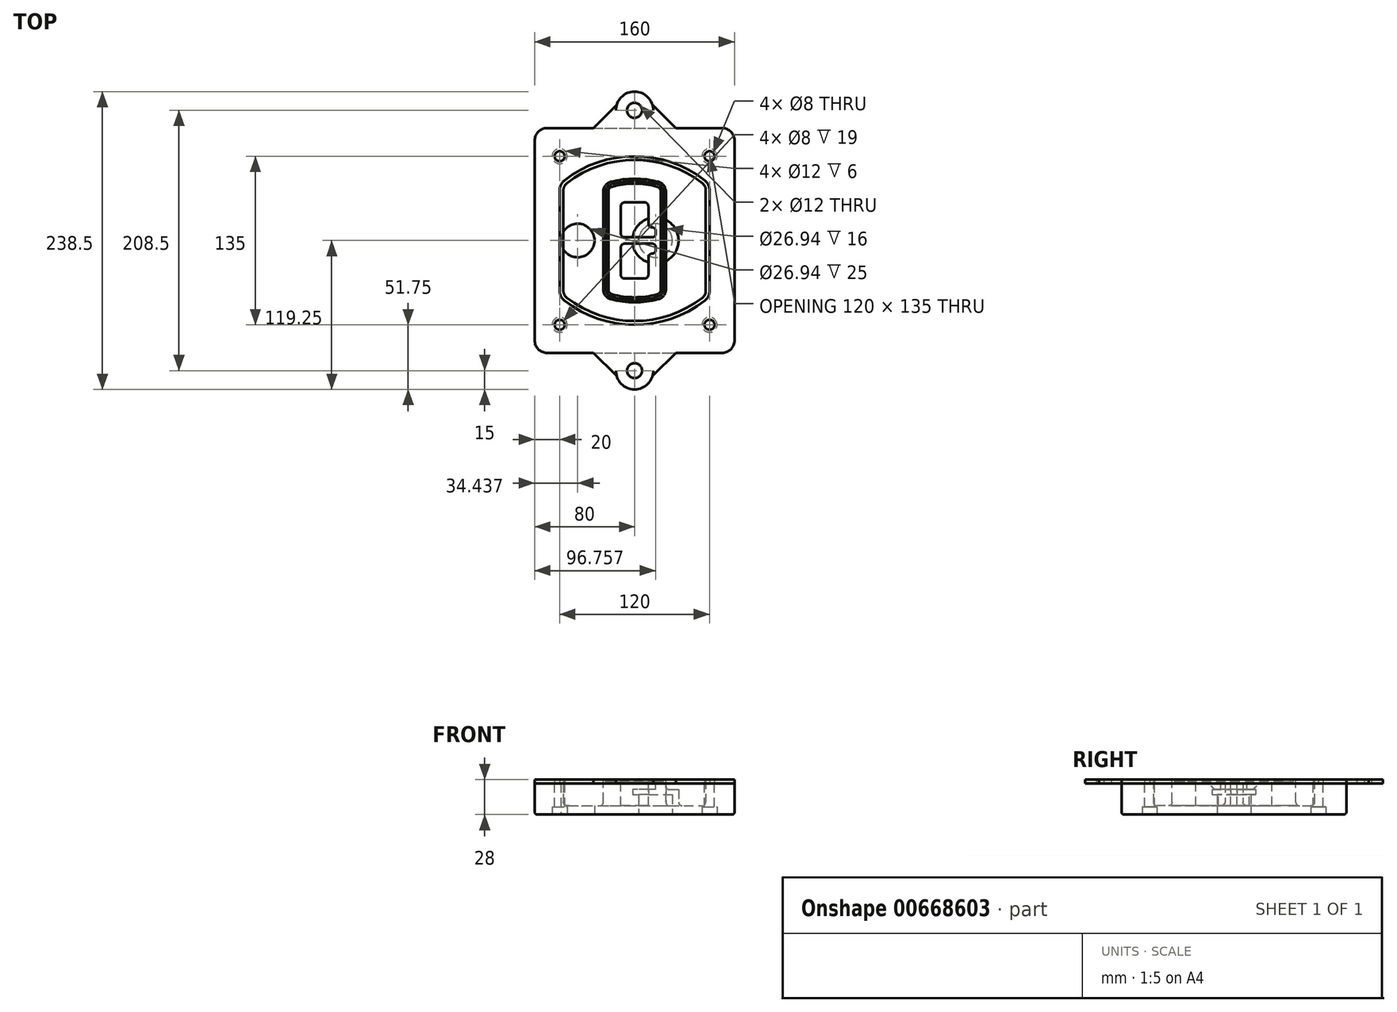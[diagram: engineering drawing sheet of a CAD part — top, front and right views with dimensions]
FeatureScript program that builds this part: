
annotation { "Feature Type Name" : "Feature", "Feature Type Description" : "" }
export const myFeature = defineFeature(function(context is Context, id is Id, definition is map)
    precondition{}
    {
        {
            var Q0;
            Q0=qCreatedBy(makeId("Top.planeOp"),FACE);
            var sketch = newSketch(context, id + "F0", { "sketchPlane" : qUnion([Q0])});
            skPoint(sketch, "E0.rect.middle", {"position": v(0, 0) * mm});
            skLineSegment(sketch, "E1.bottom", {"start": v(-70, -90) * mm, "end": v(70, -90) * mm});
            skLineSegment(sketch, "E1.top", {"start": v(-70, 90) * mm, "end": v(70, 90) * mm});
            skLineSegment(sketch, "E1.left", {"start": v(-80, -80) * mm, "end": v(-80, 80) * mm});
            skLineSegment(sketch, "E1.right", {"start": v(80, -80) * mm, "end": v(80, 80) * mm});
            skLineSegment(sketch, "E2", {"start": v(-80, 90) * mm, "end": v(80, -90) * mm, "construction": true});
            skLineSegment(sketch, "E3", {"start": v(80, 90) * mm, "end": v(-80, -90) * mm, "construction": true});
            skCircle(sketch, "E4", {"center": v(-60, 67.5) * mm, "radius": 4 * mm});
            skCircle(sketch, "E5", {"center": v(60, 67.5) * mm, "radius": 4 * mm});
            skCircle(sketch, "E6", {"center": v(60, -67.5) * mm, "radius": 4 * mm});
            skCircle(sketch, "E7", {"center": v(-60, -67.5) * mm, "radius": 4 * mm});
            skLineSegment(sketch, "E8", {"start": v(-60, 67.5) * mm, "end": v(60, 67.5) * mm, "construction": true});
            skLineSegment(sketch, "E9", {"start": v(60, 67.5) * mm, "end": v(60, -67.5) * mm, "construction": true});
            skLineSegment(sketch, "E10", {"start": v(60, -67.5) * mm, "end": v(-60, -67.5) * mm, "construction": true});
            skLineSegment(sketch, "E11", {"start": v(-60, -67.5) * mm, "end": v(-60, 67.5) * mm, "construction": true});
            skLineSegment(sketch, "E12", {"start": v(-60, 40.3) * mm, "end": v(-60, -40.3) * mm});
            skLineSegment(sketch, "E13", {"start": v(60, 40.3) * mm, "end": v(60, -40.3) * mm});
            skArc(sketch, "E14", {"start": v(56.15, 48.18) * mm, "mid": v(0, 67.5) * mm, "end": v(-56.15, 48.18) * mm});
            skArc(sketch, "E15", {"start": v(-56.15, -48.18) * mm, "mid": v(0, -67.5) * mm, "end": v(56.15, -48.18) * mm});
            skLineSegment(sketch, "E16", {"start": v(-60, 0) * mm, "end": v(60, 0) * mm, "construction": true});
            skPoint(sketch, "E17.visualSharp", {"position": v(-60, -45) * mm});
            skArc(sketch, "E17.filletArc", {"start": v(-60, -40.3) * mm, "mid": v(-58.99, -44.68) * mm, "end": v(-56.15, -48.18) * mm});
            skPoint(sketch, "E18.visualSharp", {"position": v(-60, 45) * mm});
            skArc(sketch, "E18.filletArc", {"start": v(-56.15, 48.18) * mm, "mid": v(-58.99, 44.68) * mm, "end": v(-60, 40.3) * mm});
            skPoint(sketch, "E19.visualSharp", {"position": v(60, 45) * mm});
            skArc(sketch, "E19.filletArc", {"start": v(60, 40.3) * mm, "mid": v(58.99, 44.68) * mm, "end": v(56.15, 48.18) * mm});
            skPoint(sketch, "E20.visualSharp", {"position": v(60, -45) * mm});
            skArc(sketch, "E20.filletArc", {"start": v(56.15, -48.18) * mm, "mid": v(58.99, -44.68) * mm, "end": v(60, -40.3) * mm});
            skPoint(sketch, "E21.visualSharp", {"position": v(-80, 90) * mm});
            skArc(sketch, "E21.filletArc", {"start": v(-70, 90) * mm, "mid": v(-77.07, 87.07) * mm, "end": v(-80, 80) * mm});
            skPoint(sketch, "E22.visualSharp", {"position": v(80, 90) * mm});
            skArc(sketch, "E22.filletArc", {"start": v(80, 80) * mm, "mid": v(77.07, 87.07) * mm, "end": v(70, 90) * mm});
            skPoint(sketch, "E23.visualSharp", {"position": v(80, -90) * mm});
            skArc(sketch, "E23.filletArc", {"start": v(70, -90) * mm, "mid": v(77.07, -87.07) * mm, "end": v(80, -80) * mm});
            skPoint(sketch, "E24.visualSharp", {"position": v(-80, -90) * mm});
            skArc(sketch, "E24.filletArc", {"start": v(-80, -80) * mm, "mid": v(-77.07, -87.07) * mm, "end": v(-70, -90) * mm});
            skArc(sketch, "E25.0", {"start": v(57, 40.3) * mm, "mid": v(56.3, 43.36) * mm, "end": v(54.3, 45.81) * mm});
            skLineSegment(sketch, "E25.1", {"start": v(57, 40.3) * mm, "end": v(57, -40.3) * mm});
            skArc(sketch, "E25.2", {"start": v(54.3, -45.81) * mm, "mid": v(56.3, -43.36) * mm, "end": v(57, -40.3) * mm});
            skArc(sketch, "E25.3", {"start": v(-54.3, -45.81) * mm, "mid": v(0, -64.5) * mm, "end": v(54.3, -45.81) * mm});
            skArc(sketch, "E25.4", {"start": v(-57, -40.3) * mm, "mid": v(-56.3, -43.36) * mm, "end": v(-54.3, -45.81) * mm});
            skArc(sketch, "E25.5", {"start": v(54.3, 45.81) * mm, "mid": v(0, 64.5) * mm, "end": v(-54.3, 45.81) * mm});
            skLineSegment(sketch, "E25.6", {"start": v(-57, 40.3) * mm, "end": v(-57, -40.3) * mm});
            skArc(sketch, "E25.7", {"start": v(-54.3, 45.81) * mm, "mid": v(-56.3, 43.36) * mm, "end": v(-57, 40.3) * mm});
            skArc(sketch, "E26.0", {"start": v(-58.62, 51.33) * mm, "mid": v(-62.58, 46.43) * mm, "end": v(-64, 40.3) * mm});
            skArc(sketch, "E26.1", {"start": v(58.62, 51.33) * mm, "mid": v(0, 71.5) * mm, "end": v(-58.62, 51.33) * mm});
            skArc(sketch, "E26.2", {"start": v(64, 40.3) * mm, "mid": v(62.58, 46.43) * mm, "end": v(58.62, 51.33) * mm});
            skLineSegment(sketch, "E26.3", {"start": v(64, 40.3) * mm, "end": v(64, -40.3) * mm});
            skArc(sketch, "E26.4", {"start": v(58.62, -51.33) * mm, "mid": v(62.58, -46.43) * mm, "end": v(64, -40.3) * mm});
            skLineSegment(sketch, "E26.5", {"start": v(-64, 40.3) * mm, "end": v(-64, -40.3) * mm});
            skArc(sketch, "E26.6", {"start": v(-58.62, -51.33) * mm, "mid": v(0, -71.5) * mm, "end": v(58.62, -51.33) * mm});
            skArc(sketch, "E26.7", {"start": v(-64, -40.3) * mm, "mid": v(-62.58, -46.43) * mm, "end": v(-58.62, -51.33) * mm});
            skSolve(sketch);
        }
        {
            var Q0;
            Q0=makeQuery(id+"F0.imprint","IMPRINT",FACE,{"disambiguationData":[TD([[makeQuery(id+"F0.imprint","IMPRINT",EDGE,{"derivedFrom":sQuery(id+"F0.wireOp",EDGE,"E1.bottom")}),1.0]])]});
            var Q1;
            Q1=makeQuery(id+"F0.imprint","IMPRINT",FACE,{"disambiguationData":[TD([[makeQuery(id+"F0.imprint","IMPRINT",EDGE,{"derivedFrom":sQuery(id+"F0.wireOp",EDGE,"E12")}),1.0]])]});
            var Q2;
            Q2=makeQuery(id+"F0.imprint","IMPRINT",FACE,{"disambiguationData":[TD([[makeQuery(id+"F0.imprint","IMPRINT",EDGE,{"derivedFrom":sQuery(id+"F0.wireOp",EDGE,"E25.0")}),1.0]])]});
            var Q3;
            Q3=makeQuery(id+"F0.imprint","IMPRINT",FACE,{"disambiguationData":[TD([[makeQuery(id+"F0.imprint","IMPRINT",EDGE,{"derivedFrom":sQuery(id+"F0.wireOp",EDGE,"E12")}),-1.0]])]});
            extrude(context, id + "F1", {"entities" : qUnion([Q0, Q1, Q2, Q3]), "oppositeDirection" : true, "depth" : 25 * mm});
        }
        {
            var Q0;
            Q0=makeQuery(id+"F0.imprint","IMPRINT",FACE,{"disambiguationData":[TD([[makeQuery(id+"F0.imprint","IMPRINT",EDGE,{"derivedFrom":sQuery(id+"F0.wireOp",EDGE,"E12")}),1.0]])]});
            extrude(context, id + "F2", {"entities" : qUnion([Q0]), "operationType" : NewBodyOperationType.ADD, "depth" : 3 * mm});
        }
        {
            var Q0;
            Q0=makeQuery(id+"F0.imprint","IMPRINT",FACE,{"disambiguationData":[TD([[makeQuery(id+"F0.imprint","IMPRINT",EDGE,{"derivedFrom":sQuery(id+"F0.wireOp",EDGE,"E25.0")}),1.0]])]});
            extrude(context, id + "F3", {"entities" : qUnion([Q0]), "operationType" : NewBodyOperationType.REMOVE, "oppositeDirection" : true, "depth" : 18 * mm});
        }
        {
            var Q0;
            Q0=makeQuery(id+"F2.opExtrude","CAP_FACE",FACE,{"disambiguationData":[OSD([sQuery(id+"F0.wireOp",EDGE,"E12"),sQuery(id+"F0.wireOp",EDGE,"E13"),sQuery(id+"F0.wireOp",EDGE,"E14"),sQuery(id+"F0.wireOp",EDGE,"E15"),sQuery(id+"F0.wireOp",EDGE,"E17.filletArc"),sQuery(id+"F0.wireOp",EDGE,"E18.filletArc"),sQuery(id+"F0.wireOp",EDGE,"E19.filletArc"),sQuery(id+"F0.wireOp",EDGE,"E20.filletArc"),sQuery(id+"F0.wireOp",EDGE,"E25.0"),sQuery(id+"F0.wireOp",EDGE,"E25.1"),sQuery(id+"F0.wireOp",EDGE,"E25.2"),sQuery(id+"F0.wireOp",EDGE,"E25.3"),sQuery(id+"F0.wireOp",EDGE,"E25.4"),sQuery(id+"F0.wireOp",EDGE,"E25.5"),sQuery(id+"F0.wireOp",EDGE,"E25.6"),sQuery(id+"F0.wireOp",EDGE,"E25.7")])],"isStart":false});
            var sketch = newSketch(context, id + "F4", { "sketchPlane" : qUnion([Q0])});
            skArc(sketch, "E27.0", {"start": v(-19.08, -46.97) * mm, "mid": v(0, -49.5) * mm, "end": v(19.08, -46.97) * mm});
            skArc(sketch, "E28.0", {"start": v(19.08, 46.97) * mm, "mid": v(0, 49.5) * mm, "end": v(-19.08, 46.97) * mm});
            skLineSegment(sketch, "E29", {"start": v(-25, 39.25) * mm, "end": v(-25, -39.25) * mm});
            skLineSegment(sketch, "E30", {"start": v(25, 39.25) * mm, "end": v(25, -39.25) * mm});
            skLineSegment(sketch, "E31", {"start": v(-25, 45.1) * mm, "end": v(25, 45.1) * mm, "construction": true});
            skLineSegment(sketch, "E32", {"start": v(-25, -45.1) * mm, "end": v(25, -45.1) * mm, "construction": true});
            skPoint(sketch, "E33.visualSharp", {"position": v(-25, 45.1) * mm});
            skArc(sketch, "E33.filletArc", {"start": v(-19.08, 46.97) * mm, "mid": v(-23.35, 44.11) * mm, "end": v(-25, 39.25) * mm});
            skPoint(sketch, "E34.visualSharp", {"position": v(25, 45.1) * mm});
            skArc(sketch, "E34.filletArc", {"start": v(25, 39.25) * mm, "mid": v(23.35, 44.11) * mm, "end": v(19.08, 46.97) * mm});
            skPoint(sketch, "E35.visualSharp", {"position": v(25, -45.1) * mm});
            skArc(sketch, "E35.filletArc", {"start": v(19.08, -46.97) * mm, "mid": v(23.35, -44.11) * mm, "end": v(25, -39.25) * mm});
            skPoint(sketch, "E36.visualSharp", {"position": v(-25, -45.1) * mm});
            skArc(sketch, "E36.filletArc", {"start": v(-25, -39.25) * mm, "mid": v(-23.35, -44.11) * mm, "end": v(-19.08, -46.97) * mm});
            skArc(sketch, "E37.0", {"start": v(54.3, 45.81) * mm, "mid": v(0, 64.5) * mm, "end": v(-54.3, 45.81) * mm});
            skArc(sketch, "E37.1", {"start": v(-54.3, 45.81) * mm, "mid": v(-56.3, 43.36) * mm, "end": v(-57, 40.3) * mm});
            skLineSegment(sketch, "E37.2", {"start": v(-57, 40.3) * mm, "end": v(-57, -40.3) * mm});
            skArc(sketch, "E37.3", {"start": v(-57, -40.3) * mm, "mid": v(-56.3, -43.36) * mm, "end": v(-54.3, -45.81) * mm});
            skArc(sketch, "E37.4", {"start": v(-54.3, -45.81) * mm, "mid": v(0, -64.5) * mm, "end": v(54.3, -45.81) * mm});
            skArc(sketch, "E37.5", {"start": v(54.3, -45.81) * mm, "mid": v(56.3, -43.36) * mm, "end": v(57, -40.3) * mm});
            skLineSegment(sketch, "E37.6", {"start": v(57, 40.3) * mm, "end": v(57, -40.3) * mm});
            skArc(sketch, "E37.7", {"start": v(57, 40.3) * mm, "mid": v(56.3, 43.36) * mm, "end": v(54.3, 45.81) * mm});
            skLineSegment(sketch, "E38.0", {"start": v(23, 39.25) * mm, "end": v(23, -39.25) * mm});
            skArc(sketch, "E38.1", {"start": v(18.56, -45.04) * mm, "mid": v(21.76, -42.9) * mm, "end": v(23, -39.25) * mm});
            skArc(sketch, "E38.2", {"start": v(-18.56, -45.04) * mm, "mid": v(0, -47.5) * mm, "end": v(18.56, -45.04) * mm});
            skArc(sketch, "E38.3", {"start": v(-23, -39.25) * mm, "mid": v(-21.76, -42.9) * mm, "end": v(-18.56, -45.04) * mm});
            skLineSegment(sketch, "E38.4", {"start": v(-23, 39.25) * mm, "end": v(-23, -39.25) * mm});
            skArc(sketch, "E38.5", {"start": v(23, 39.25) * mm, "mid": v(21.76, 42.9) * mm, "end": v(18.56, 45.04) * mm});
            skArc(sketch, "E38.6", {"start": v(-18.56, 45.04) * mm, "mid": v(-21.76, 42.9) * mm, "end": v(-23, 39.25) * mm});
            skArc(sketch, "E38.7", {"start": v(18.56, 45.04) * mm, "mid": v(0, 47.5) * mm, "end": v(-18.56, 45.04) * mm});
            skArc(sketch, "E39.0", {"start": v(21, 39.25) * mm, "mid": v(20.18, 41.68) * mm, "end": v(18.04, 43.1) * mm});
            skLineSegment(sketch, "E39.1", {"start": v(21, 39.25) * mm, "end": v(21, -39.25) * mm});
            skArc(sketch, "E39.2", {"start": v(18.04, -43.1) * mm, "mid": v(20.18, -41.68) * mm, "end": v(21, -39.25) * mm});
            skArc(sketch, "E39.3", {"start": v(-18.04, -43.1) * mm, "mid": v(0, -45.5) * mm, "end": v(18.04, -43.1) * mm});
            skArc(sketch, "E39.4", {"start": v(-21, -39.25) * mm, "mid": v(-20.18, -41.68) * mm, "end": v(-18.04, -43.1) * mm});
            skArc(sketch, "E39.5", {"start": v(18.04, 43.1) * mm, "mid": v(0, 45.5) * mm, "end": v(-18.04, 43.1) * mm});
            skLineSegment(sketch, "E39.6", {"start": v(-21, 39.25) * mm, "end": v(-21, -39.25) * mm});
            skArc(sketch, "E39.7", {"start": v(-18.04, 43.1) * mm, "mid": v(-20.18, 41.68) * mm, "end": v(-21, 39.25) * mm});
            skLineSegment(sketch, "E40", {"start": v(-25, 0) * mm, "end": v(25, 0) * mm, "construction": true});
            skLineSegment(sketch, "E41", {"start": v(-11, 5.5) * mm, "end": v(-11, 27.5) * mm});
            skLineSegment(sketch, "E42", {"start": v(-8, 30.5) * mm, "end": v(8, 30.5) * mm});
            skLineSegment(sketch, "E43", {"start": v(11, 27.5) * mm, "end": v(11, 13.5) * mm});
            skLineSegment(sketch, "E44", {"start": v(14, 10.5) * mm, "end": v(14, 10.5) * mm});
            skLineSegment(sketch, "E45", {"start": v(17, 7.5) * mm, "end": v(17, 5.5) * mm});
            skLineSegment(sketch, "E46", {"start": v(14, 2.5) * mm, "end": v(-8, 2.5) * mm});
            skPoint(sketch, "E47.visualSharp", {"position": v(-11, 30.5) * mm});
            skArc(sketch, "E47.filletArc", {"start": v(-8, 30.5) * mm, "mid": v(-10.12, 29.62) * mm, "end": v(-11, 27.5) * mm});
            skPoint(sketch, "E48.visualSharp", {"position": v(11, 30.5) * mm});
            skArc(sketch, "E48.filletArc", {"start": v(11, 27.5) * mm, "mid": v(10.12, 29.62) * mm, "end": v(8, 30.5) * mm});
            skPoint(sketch, "E49.visualSharp", {"position": v(11, 10.5) * mm});
            skArc(sketch, "E49.filletArc", {"start": v(11, 13.5) * mm, "mid": v(11.88, 11.38) * mm, "end": v(14, 10.5) * mm});
            skPoint(sketch, "E50.visualSharp", {"position": v(17, 10.5) * mm});
            skArc(sketch, "E50.filletArc", {"start": v(17, 7.5) * mm, "mid": v(16.12, 9.62) * mm, "end": v(14, 10.5) * mm});
            skPoint(sketch, "E51.visualSharp", {"position": v(17, 2.5) * mm});
            skArc(sketch, "E51.filletArc", {"start": v(14, 2.5) * mm, "mid": v(16.12, 3.38) * mm, "end": v(17, 5.5) * mm});
            skPoint(sketch, "E52.visualSharp", {"position": v(-11, 2.5) * mm});
            skArc(sketch, "E52.filletArc", {"start": v(-11, 5.5) * mm, "mid": v(-10.12, 3.38) * mm, "end": v(-8, 2.5) * mm});
            skLineSegment(sketch, "E53.0.MirrorCS", {"start": v(14, -2.5) * mm, "end": v(-8, -2.5) * mm});
            skArc(sketch, "E54.0.MirrorCS", {"start": v(-11, -5.5) * mm, "mid": v(-10.12, -3.38) * mm, "end": v(-8, -2.5) * mm});
            skLineSegment(sketch, "E55.0.MirrorCS", {"start": v(-11, -5.5) * mm, "end": v(-11, -27.5) * mm});
            skArc(sketch, "E56.0.MirrorCS", {"start": v(-8, -30.5) * mm, "mid": v(-10.12, -29.62) * mm, "end": v(-11, -27.5) * mm});
            skLineSegment(sketch, "E57.0.MirrorCS", {"start": v(-8, -30.5) * mm, "end": v(8, -30.5) * mm});
            skArc(sketch, "E58.0.MirrorCS", {"start": v(11, -27.5) * mm, "mid": v(10.12, -29.62) * mm, "end": v(8, -30.5) * mm});
            skLineSegment(sketch, "E59.0.MirrorCS", {"start": v(11, -27.5) * mm, "end": v(11, -13.5) * mm});
            skArc(sketch, "E60.0.MirrorCS", {"start": v(11, -13.5) * mm, "mid": v(11.88, -11.38) * mm, "end": v(14, -10.5) * mm});
            skArc(sketch, "E61.0.MirrorCS", {"start": v(17, -7.5) * mm, "mid": v(16.12, -9.62) * mm, "end": v(14, -10.5) * mm});
            skLineSegment(sketch, "E62.0.MirrorCS", {"start": v(17, -7.5) * mm, "end": v(17, -5.5) * mm});
            skArc(sketch, "E63.0.MirrorCS", {"start": v(14, -2.5) * mm, "mid": v(16.12, -3.38) * mm, "end": v(17, -5.5) * mm});
            skSolve(sketch);
        }
        {
            var Q0;
            Q0=makeQuery(id+"F4.imprint","IMPRINT",FACE,{"disambiguationData":[TD([[makeQuery(id+"F4.imprint","IMPRINT",EDGE,{"derivedFrom":sQuery(id+"F4.wireOp",EDGE,"E27.0")}),1.0]])]});
            var Q1;
            Q1=makeQuery(id+"F4.imprint","IMPRINT",FACE,{"disambiguationData":[TD([[makeQuery(id+"F4.imprint","IMPRINT",EDGE,{"derivedFrom":sQuery(id+"F4.wireOp",EDGE,"E38.0")}),-1.0]])]});
            var Q2;
            Q2=makeQuery(id+"F4.imprint","IMPRINT",FACE,{"disambiguationData":[TD([[makeQuery(id+"F4.imprint","IMPRINT",EDGE,{"derivedFrom":sQuery(id+"F4.wireOp",EDGE,"E39.0")}),1.0]])]});
            extrude(context, id + "F5", {"entities" : qUnion([Q0, Q1, Q2]), "operationType" : NewBodyOperationType.ADD, "endBound" : BoundingType.UP_TO_NEXT, "oppositeDirection" : true, "depth" : 25 * mm});
        }
        {
            var Q0;
            Q0=makeQuery(id+"F4.imprint","IMPRINT",FACE,{"disambiguationData":[TD([[makeQuery(id+"F4.imprint","IMPRINT",EDGE,{"derivedFrom":sQuery(id+"F4.wireOp",EDGE,"E38.0")}),-1.0]])]});
            extrude(context, id + "F6", {"entities" : qUnion([Q0]), "operationType" : NewBodyOperationType.REMOVE, "oppositeDirection" : true, "depth" : 2 * mm});
        }
        {
            var Q0;
            Q0=makeQuery(id+"F1.opExtrude","CAP_FACE",FACE,{"disambiguationData":[OSD([sQuery(id+"F0.wireOp",EDGE,"E1.bottom"),sQuery(id+"F0.wireOp",EDGE,"E1.top"),sQuery(id+"F0.wireOp",EDGE,"E1.left"),sQuery(id+"F0.wireOp",EDGE,"E1.right"),sQuery(id+"F0.wireOp",EDGE,"E4"),sQuery(id+"F0.wireOp",EDGE,"E5"),sQuery(id+"F0.wireOp",EDGE,"E6"),sQuery(id+"F0.wireOp",EDGE,"E7"),sQuery(id+"F0.wireOp",EDGE,"E21.filletArc"),sQuery(id+"F0.wireOp",EDGE,"E22.filletArc"),sQuery(id+"F0.wireOp",EDGE,"E23.filletArc"),sQuery(id+"F0.wireOp",EDGE,"E24.filletArc")])],"isStart":false});
            var sketch = newSketch(context, id + "F7", { "sketchPlane" : qUnion([Q0])});
            skCircle(sketch, "E64", {"center": v(16.76, 0) * mm, "radius": 13.47 * mm});
            skCircle(sketch, "E65", {"center": v(-45.56, 0) * mm, "radius": 13.47 * mm});
            skLineSegment(sketch, "E66", {"start": v(80, 0) * mm, "end": v(-80, 0) * mm});
            skCircle(sketch, "E67", {"center": v(16.76, 0) * mm, "radius": 18.47 * mm});
            skCircle(sketch, "E68", {"center": v(60, -67.5) * mm, "radius": 6 * mm});
            skCircle(sketch, "E69", {"center": v(-60, -67.5) * mm, "radius": 6 * mm});
            skCircle(sketch, "E70", {"center": v(-60, 67.5) * mm, "radius": 6 * mm});
            skCircle(sketch, "E71", {"center": v(60, 67.5) * mm, "radius": 6 * mm});
            skSolve(sketch);
        }
        {
            var Q0;
            {var subQ1=sQuery(id+"F7.wireOp",EDGE,"E66");var subQ4=sQuery(id+"F7.wireOp",EDGE,"E64");var subQ6=makeQuery(id+"F7.imprint","INTERSECT",VERTEX,{"disambiguationData":[OD(0.0)],"derivedFrom":[subQ4,subQ1]});Q0=makeQuery(id+"F7.imprint","IMPRINT",FACE,{"disambiguationData":[TD([[makeQuery(id+"F7.imprint","IMPRINT",EDGE,{"disambiguationData":[TD([[subQ6,-1.0]])],"derivedFrom":subQ4}),-1.0]])]});}
            var Q1;
            {var subQ0=sQuery(id+"F7.wireOp",EDGE,"E66");var subQ1=sQuery(id+"F7.wireOp",EDGE,"E64");var subQ3=makeQuery(id+"F7.imprint","INTERSECT",VERTEX,{"disambiguationData":[OD(0.0)],"derivedFrom":[subQ1,subQ0]});Q1=makeQuery(id+"F7.imprint","IMPRINT",FACE,{"disambiguationData":[TD([[makeQuery(id+"F7.imprint","IMPRINT",EDGE,{"disambiguationData":[TD([[subQ3,-1.0]])],"derivedFrom":subQ1}),1.0]])]});}
            var Q2;
            {var subQ0=sQuery(id+"F7.wireOp",EDGE,"E66");var subQ1=sQuery(id+"F7.wireOp",EDGE,"E64");var subQ3=makeQuery(id+"F7.imprint","INTERSECT",VERTEX,{"disambiguationData":[OD(0.0)],"derivedFrom":[subQ1,subQ0]});Q2=makeQuery(id+"F7.imprint","IMPRINT",FACE,{"disambiguationData":[TD([[makeQuery(id+"F7.imprint","IMPRINT",EDGE,{"disambiguationData":[TD([[subQ3,1.0]])],"derivedFrom":subQ1}),1.0]])]});}
            var Q3;
            {var subQ1=sQuery(id+"F7.wireOp",EDGE,"E66");var subQ4=sQuery(id+"F7.wireOp",EDGE,"E64");var subQ6=makeQuery(id+"F7.imprint","INTERSECT",VERTEX,{"disambiguationData":[OD(0.0)],"derivedFrom":[subQ4,subQ1]});Q3=makeQuery(id+"F7.imprint","IMPRINT",FACE,{"disambiguationData":[TD([[makeQuery(id+"F7.imprint","IMPRINT",EDGE,{"disambiguationData":[TD([[subQ6,1.0]])],"derivedFrom":subQ4}),-1.0]])]});}
            extrude(context, id + "F8", {"entities" : qUnion([Q0, Q1, Q2, Q3]), "operationType" : NewBodyOperationType.ADD, "oppositeDirection" : true, "depth" : 20 * mm});
        }
        {
            var Q0;
            {var subQ0=sQuery(id+"F7.wireOp",EDGE,"E66");var subQ1=sQuery(id+"F7.wireOp",EDGE,"E64");var subQ3=makeQuery(id+"F7.imprint","INTERSECT",VERTEX,{"disambiguationData":[OD(0.0)],"derivedFrom":[subQ1,subQ0]});Q0=makeQuery(id+"F7.imprint","IMPRINT",FACE,{"disambiguationData":[TD([[makeQuery(id+"F7.imprint","IMPRINT",EDGE,{"disambiguationData":[TD([[subQ3,-1.0]])],"derivedFrom":subQ1}),1.0]])]});}
            var Q1;
            {var subQ0=sQuery(id+"F7.wireOp",EDGE,"E66");var subQ1=sQuery(id+"F7.wireOp",EDGE,"E64");var subQ3=makeQuery(id+"F7.imprint","INTERSECT",VERTEX,{"disambiguationData":[OD(0.0)],"derivedFrom":[subQ1,subQ0]});Q1=makeQuery(id+"F7.imprint","IMPRINT",FACE,{"disambiguationData":[TD([[makeQuery(id+"F7.imprint","IMPRINT",EDGE,{"disambiguationData":[TD([[subQ3,1.0]])],"derivedFrom":subQ1}),1.0]])]});}
            extrude(context, id + "F9", {"entities" : qUnion([Q0, Q1]), "operationType" : NewBodyOperationType.REMOVE, "oppositeDirection" : true, "depth" : 16 * mm});
        }
        {
            var Q0;
            {var subQ0=sQuery(id+"F7.wireOp",EDGE,"E66");var subQ1=sQuery(id+"F7.wireOp",EDGE,"E65");var subQ3=makeQuery(id+"F7.imprint","INTERSECT",VERTEX,{"disambiguationData":[OD(0.0)],"derivedFrom":[subQ1,subQ0]});Q0=makeQuery(id+"F7.imprint","IMPRINT",FACE,{"disambiguationData":[TD([[makeQuery(id+"F7.imprint","IMPRINT",EDGE,{"disambiguationData":[TD([[subQ3,-1.0]])],"derivedFrom":subQ1}),1.0]])]});}
            var Q1;
            {var subQ0=sQuery(id+"F7.wireOp",EDGE,"E66");var subQ1=sQuery(id+"F7.wireOp",EDGE,"E65");var subQ3=makeQuery(id+"F7.imprint","INTERSECT",VERTEX,{"disambiguationData":[OD(0.0)],"derivedFrom":[subQ1,subQ0]});Q1=makeQuery(id+"F7.imprint","IMPRINT",FACE,{"disambiguationData":[TD([[makeQuery(id+"F7.imprint","IMPRINT",EDGE,{"disambiguationData":[TD([[subQ3,1.0]])],"derivedFrom":subQ1}),1.0]])]});}
            extrude(context, id + "F10", {"entities" : qUnion([Q0, Q1]), "operationType" : NewBodyOperationType.REMOVE, "oppositeDirection" : true, "depth" : 25 * mm});
        }
        {
            var Q0;
            Q0=makeQuery(id+"F7.imprint","IMPRINT",FACE,{"disambiguationData":[TD([[makeQuery(id+"F7.imprint","IMPRINT",EDGE,{"derivedFrom":sQuery(id+"F7.wireOp",EDGE,"E68")}),1.0]])]});
            var Q1;
            Q1=makeQuery(id+"F7.imprint","IMPRINT",FACE,{"disambiguationData":[TD([[makeQuery(id+"F7.imprint","IMPRINT",EDGE,{"derivedFrom":makeQuery(id+"F1.opExtrude","CAP_EDGE",EDGE,{"disambiguationData":[OSD([sQuery(id+"F0.wireOp",EDGE,"E5")])],"isStart":false})}),-1.0]])]});
            var Q2;
            Q2=makeQuery(id+"F7.imprint","IMPRINT",FACE,{"disambiguationData":[TD([[makeQuery(id+"F7.imprint","IMPRINT",EDGE,{"derivedFrom":sQuery(id+"F7.wireOp",EDGE,"E69")}),1.0]])]});
            var Q3;
            Q3=makeQuery(id+"F7.imprint","IMPRINT",FACE,{"disambiguationData":[TD([[makeQuery(id+"F7.imprint","IMPRINT",EDGE,{"derivedFrom":makeQuery(id+"F1.opExtrude","CAP_EDGE",EDGE,{"disambiguationData":[OSD([sQuery(id+"F0.wireOp",EDGE,"E4")])],"isStart":false})}),-1.0]])]});
            var Q4;
            Q4=makeQuery(id+"F7.imprint","IMPRINT",FACE,{"disambiguationData":[TD([[makeQuery(id+"F7.imprint","IMPRINT",EDGE,{"derivedFrom":sQuery(id+"F7.wireOp",EDGE,"E70")}),1.0]])]});
            var Q5;
            Q5=makeQuery(id+"F7.imprint","IMPRINT",FACE,{"disambiguationData":[TD([[makeQuery(id+"F7.imprint","IMPRINT",EDGE,{"derivedFrom":makeQuery(id+"F1.opExtrude","CAP_EDGE",EDGE,{"disambiguationData":[OSD([sQuery(id+"F0.wireOp",EDGE,"E7")])],"isStart":false})}),-1.0]])]});
            var Q6;
            Q6=makeQuery(id+"F7.imprint","IMPRINT",FACE,{"disambiguationData":[TD([[makeQuery(id+"F7.imprint","IMPRINT",EDGE,{"derivedFrom":sQuery(id+"F7.wireOp",EDGE,"E71")}),1.0]])]});
            var Q7;
            Q7=makeQuery(id+"F7.imprint","IMPRINT",FACE,{"disambiguationData":[TD([[makeQuery(id+"F7.imprint","IMPRINT",EDGE,{"derivedFrom":makeQuery(id+"F1.opExtrude","CAP_EDGE",EDGE,{"disambiguationData":[OSD([sQuery(id+"F0.wireOp",EDGE,"E6")])],"isStart":false})}),-1.0]])]});
            extrude(context, id + "F11", {"entities" : qUnion([Q0, Q1, Q2, Q3, Q4, Q5, Q6, Q7]), "operationType" : NewBodyOperationType.REMOVE, "oppositeDirection" : true, "depth" : 6 * mm});
        }
        {
            var Q0;
            Q0=makeQuery(id+"F9.boolean.opBoolean","COPY",FACE,{"derivedFrom":makeQuery(id+"F9.opExtrude","CAP_FACE",FACE,{"disambiguationData":[OSD([sQuery(id+"F7.wireOp",EDGE,"E64")])],"isStart":false})});
            var sketch = newSketch(context, id + "F12", { "sketchPlane" : qUnion([Q0])});
            skArc(sketch, "E72.0", {"start": v(11, 17.55) * mm, "mid": v(2.57, 11.82) * mm, "end": v(-1.54, 2.5) * mm});
            skArc(sketch, "E72.1", {"start": v(-1.54, -2.5) * mm, "mid": v(2.57, -11.82) * mm, "end": v(11, -17.55) * mm});
            skLineSegment(sketch, "E73", {"start": v(-1.54, -2.5) * mm, "end": v(14, -2.5) * mm});
            skLineSegment(sketch, "E74.0", {"start": v(14, 2.5) * mm, "end": v(-1.54, 2.5) * mm});
            skArc(sketch, "E74.1", {"start": v(14, 2.5) * mm, "mid": v(16.12, 3.38) * mm, "end": v(17, 5.5) * mm});
            skLineSegment(sketch, "E74.2", {"start": v(17, 7.5) * mm, "end": v(17, 5.5) * mm});
            skArc(sketch, "E74.3", {"start": v(17, 7.5) * mm, "mid": v(16.12, 9.62) * mm, "end": v(14, 10.5) * mm});
            skArc(sketch, "E74.4", {"start": v(11, 13.5) * mm, "mid": v(11.88, 11.38) * mm, "end": v(14, 10.5) * mm});
            skLineSegment(sketch, "E74.5", {"start": v(11, 17.55) * mm, "end": v(11, 13.5) * mm});
            skLineSegment(sketch, "E74.7", {"start": v(14, -2.5) * mm, "end": v(-1.54, -2.5) * mm});
            skArc(sketch, "E74.8", {"start": v(14, -2.5) * mm, "mid": v(16.12, -3.38) * mm, "end": v(17, -5.5) * mm});
            skLineSegment(sketch, "E74.9", {"start": v(17, -7.5) * mm, "end": v(17, -5.5) * mm});
            skArc(sketch, "E74.10", {"start": v(17, -7.5) * mm, "mid": v(16.12, -9.62) * mm, "end": v(14, -10.5) * mm});
            skArc(sketch, "E74.11", {"start": v(11, -13.5) * mm, "mid": v(11.88, -11.38) * mm, "end": v(14, -10.5) * mm});
            skLineSegment(sketch, "E74.12", {"start": v(11, -17.55) * mm, "end": v(11, -13.5) * mm});
            skPoint(sketch, "E75.orphan", {"position": v(11, -27.5) * mm});
            skPoint(sketch, "E76.orphan", {"position": v(-8, -2.5) * mm});
            skPoint(sketch, "E77.orphan", {"position": v(-8, 2.5) * mm});
            skPoint(sketch, "E78.orphan", {"position": v(11, 27.5) * mm});
            skSolve(sketch);
        }
        {
            var Q0;
            {var subQ7=sQuery(id+"F12.wireOp",EDGE,"E72.0");var subQ14=sQuery(id+"F12.wireOp",EDGE,"E72.1");var subQ16=sQuery(id+"F12.wireOp",EDGE,"E74.1");var subQ18=sQuery(id+"F12.wireOp",EDGE,"E74.8");Q0=qUnion([makeQuery(id+"F12.imprint","IMPRINT",FACE,{"disambiguationData":[TD([[makeQuery(id+"F12.imprint","IMPRINT",EDGE,{"derivedFrom":subQ7}),1.0]])]}),makeQuery(id+"F12.imprint","IMPRINT",FACE,{"disambiguationData":[TD([[makeQuery(id+"F12.imprint","IMPRINT",EDGE,{"derivedFrom":subQ14}),1.0]])]}),makeQuery(id+"F12.imprint","IMPRINT",FACE,{"disambiguationData":[TD([[makeQuery(id+"F12.imprint","IMPRINT",EDGE,{"derivedFrom":subQ16}),1.0]])]}),makeQuery(id+"F12.imprint","IMPRINT",FACE,{"disambiguationData":[TD([[makeQuery(id+"F12.imprint","IMPRINT",EDGE,{"derivedFrom":subQ18}),-1.0]])]})]);}
            var Q1;
            Q1=makeQuery(id+"F5.boolean.opBoolean","SPLIT",FACE,{"disambiguationData":[TD([makeQuery(id+"F5.opExtrude","SWEPT_FACE",FACE,{"disambiguationData":[OSD([sQuery(id+"F4.wireOp",EDGE,"E41")])]})])],"derivedFrom":makeQuery(id+"F3.boolean.opBoolean","COPY",FACE,{"derivedFrom":makeQuery(id+"F3.opExtrude","CAP_FACE",FACE,{"disambiguationData":[OSD([sQuery(id+"F0.wireOp",EDGE,"E25.0"),sQuery(id+"F0.wireOp",EDGE,"E25.1"),sQuery(id+"F0.wireOp",EDGE,"E25.2"),sQuery(id+"F0.wireOp",EDGE,"E25.3"),sQuery(id+"F0.wireOp",EDGE,"E25.4"),sQuery(id+"F0.wireOp",EDGE,"E25.5"),sQuery(id+"F0.wireOp",EDGE,"E25.6"),sQuery(id+"F0.wireOp",EDGE,"E25.7")])],"isStart":false})})});
            extrude(context, id + "F13", {"entities" : qUnion([Q0]), "operationType" : NewBodyOperationType.REMOVE, "endBound" : BoundingType.UP_TO_SURFACE, "endBoundEntityFace" : qUnion([Q1]), "depth" : 25 * mm});
        }
        {
            var Q0;
            Q0=makeQuery(id+"F3.boolean.opBoolean","COPY",EDGE,{"derivedFrom":makeQuery(id+"F3.opExtrude","CAP_EDGE",EDGE,{"disambiguationData":[OSD([sQuery(id+"F0.wireOp",EDGE,"E25.6")])],"isStart":false})});
            var Q1;
            Q1=makeQuery(id+"F8.boolean.opBoolean","INTERSECT",EDGE,{"derivedFrom":[makeQuery(id+"F5.opExtrude","SWEPT_FACE",FACE,{"disambiguationData":[OSD([sQuery(id+"F4.wireOp",EDGE,"E30")])]}),makeQuery(id+"F8.opExtrude","CAP_FACE",FACE,{"disambiguationData":[OSD([sQuery(id+"F7.wireOp",EDGE,"E67")])],"isStart":false})]});
            var Q2;
            Q2=makeQuery(id+"F8.boolean.opBoolean","INTERSECT",EDGE,{"disambiguationData":[OD(1.0)],"derivedFrom":[makeQuery(id+"F5.opExtrude","SWEPT_FACE",FACE,{"disambiguationData":[OSD([sQuery(id+"F4.wireOp",EDGE,"E30")])]}),makeQuery(id+"F8.opExtrude","SWEPT_FACE",FACE,{"disambiguationData":[OSD([sQuery(id+"F7.wireOp",EDGE,"E67")])]})]});
            var Q3;
            {var subQ0=sQuery(id+"F4.wireOp",EDGE,"E30");Q3=makeQuery(id+"F8.boolean.opBoolean","SPLIT",EDGE,{"disambiguationData":[TD([makeQuery(id+"F5.opExtrude","SWEPT_FACE",FACE,{"disambiguationData":[OSD([sQuery(id+"F4.wireOp",EDGE,"E35.filletArc")])]})])],"derivedFrom":makeQuery(id+"F5.opExtrude","CAP_EDGE",EDGE,{"disambiguationData":[OSD([subQ0])],"isStart":false})});}
            var Q4;
            {var subQ0=sQuery(id+"F0.wireOp",EDGE,"E25.7");var subQ1=sQuery(id+"F0.wireOp",EDGE,"E25.1");var subQ2=sQuery(id+"F0.wireOp",EDGE,"E25.6");var subQ3=sQuery(id+"F0.wireOp",EDGE,"E25.5");var subQ4=sQuery(id+"F0.wireOp",EDGE,"E25.4");var subQ5=sQuery(id+"F0.wireOp",EDGE,"E25.0");var subQ6=sQuery(id+"F0.wireOp",EDGE,"E25.2");var subQ7=sQuery(id+"F0.wireOp",EDGE,"E25.3");Q4=makeQuery(id+"F8.boolean.opBoolean","INTERSECT",EDGE,{"derivedFrom":[makeQuery(id+"F5.boolean.opBoolean","SPLIT",FACE,{"disambiguationData":[TD([makeQuery(id+"F2.opExtrude","SWEPT_FACE",FACE,{"disambiguationData":[OSD([subQ5])]})])],"derivedFrom":makeQuery(id+"F3.boolean.opBoolean","COPY",FACE,{"derivedFrom":makeQuery(id+"F3.opExtrude","CAP_FACE",FACE,{"disambiguationData":[OSD([subQ5,subQ1,subQ6,subQ7,subQ4,subQ3,subQ2,subQ0])],"isStart":false})})}),makeQuery(id+"F8.opExtrude","SWEPT_FACE",FACE,{"disambiguationData":[OSD([sQuery(id+"F7.wireOp",EDGE,"E67")])]})]});}
            var Q5;
            Q5=makeQuery(id+"F8.boolean.opBoolean","INTERSECT",EDGE,{"disambiguationData":[OD(0.0)],"derivedFrom":[makeQuery(id+"F5.opExtrude","SWEPT_FACE",FACE,{"disambiguationData":[OSD([sQuery(id+"F4.wireOp",EDGE,"E30")])]}),makeQuery(id+"F8.opExtrude","SWEPT_FACE",FACE,{"disambiguationData":[OSD([sQuery(id+"F7.wireOp",EDGE,"E67")])]})]});
            fillet(context, id + "F14", {"entities" : qUnion([Q0, Q1, Q2, Q3, Q4, Q5]), "radius" : 3 * mm, "tangentPropagation" : true, "allowEdgeOverflow" : false});
        }
        {
            var Q0;
            Q0=makeQuery(id+"F1.opExtrude","CAP_EDGE",EDGE,{"disambiguationData":[OSD([sQuery(id+"F0.wireOp",EDGE,"E1.bottom")])],"isStart":false});
            fillet(context, id + "F15", {"entities" : qUnion([Q0]), "radius" : 2 * mm, "tangentPropagation" : true, "allowEdgeOverflow" : false});
        }
        {
            var Q0;
            {var subQ0=sQuery(id+"F0.wireOp",EDGE,"E21.filletArc");var subQ1=sQuery(id+"F0.wireOp",EDGE,"E7");var subQ2=sQuery(id+"F0.wireOp",EDGE,"E6");var subQ3=sQuery(id+"F0.wireOp",EDGE,"E5");var subQ4=sQuery(id+"F0.wireOp",EDGE,"E4");var subQ5=sQuery(id+"F0.wireOp",EDGE,"E22.filletArc");var subQ6=sQuery(id+"F0.wireOp",EDGE,"E1.bottom");var subQ7=sQuery(id+"F0.wireOp",EDGE,"E1.right");var subQ8=sQuery(id+"F0.wireOp",EDGE,"E1.top");var subQ9=sQuery(id+"F0.wireOp",EDGE,"E1.left");var subQ10=sQuery(id+"F0.wireOp",EDGE,"E23.filletArc");var subQ11=sQuery(id+"F0.wireOp",EDGE,"E24.filletArc");Q0=makeQuery(id+"F2.boolean.opBoolean","SPLIT",FACE,{"disambiguationData":[TD([makeQuery(id+"F1.opExtrude","SWEPT_FACE",FACE,{"disambiguationData":[OSD([subQ6])]})])],"derivedFrom":makeQuery(id+"F1.opExtrude","CAP_FACE",FACE,{"disambiguationData":[OSD([subQ6,subQ8,subQ9,subQ7,subQ4,subQ3,subQ2,subQ1,subQ0,subQ5,subQ10,subQ11])],"isStart":true})});}
            var sketch = newSketch(context, id + "F16", { "sketchPlane" : qUnion([Q0])});
            skLineSegment(sketch, "E79", {"start": v(0, 90) * mm, "end": v(0, 104.25) * mm, "construction": true});
            skCircle(sketch, "E80", {"center": v(0, 104.25) * mm, "radius": 6 * mm});
            skArc(sketch, "E81", {"start": v(15, 104.25) * mm, "mid": v(0, 119.25) * mm, "end": v(-15, 104.25) * mm});
            skLineSegment(sketch, "E82", {"start": v(-15, 108) * mm, "end": v(-15, 104.25) * mm});
            skLineSegment(sketch, "E83", {"start": v(15, 108) * mm, "end": v(15, 104.25) * mm});
            skLineSegment(sketch, "E84", {"start": v(-15, 108) * mm, "end": v(-33, 90) * mm});
            skLineSegment(sketch, "E85", {"start": v(15, 108) * mm, "end": v(33, 90) * mm});
            skPoint(sketch, "E86.orphan", {"position": v(-15, 90) * mm});
            skPoint(sketch, "E87.orphan", {"position": v(15, 90) * mm});
            skLineSegment(sketch, "E88", {"start": v(-80, 0) * mm, "end": v(80, 0) * mm, "construction": true});
            skLineSegment(sketch, "E89.MirrorCS", {"start": v(-15, -108) * mm, "end": v(-33, -90) * mm});
            skLineSegment(sketch, "E90.MirrorCS", {"start": v(15, -108) * mm, "end": v(33, -90) * mm});
            skLineSegment(sketch, "E91.MirrorCS", {"start": v(15, -108) * mm, "end": v(15, -104.25) * mm});
            skLineSegment(sketch, "E92.MirrorCS", {"start": v(-15, -108) * mm, "end": v(-15, -104.25) * mm});
            skArc(sketch, "E93.MirrorCS", {"start": v(15, -104.25) * mm, "mid": v(0, -119.25) * mm, "end": v(-15, -104.25) * mm});
            skCircle(sketch, "E94.MirrorC", {"center": v(0, -104.25) * mm, "radius": 6 * mm});
            skText(sketch, "E95", { "text": "Samantha Herkins 48,030.408 mm^3", "fontName": "OpenSans-Regular.ttf"});
            const initialGuessF16  = {"E95": [-0.14048, -0.16265, 1, 0, 0.02615]};
            skSetInitialGuess(sketch, initialGuessF16);
            skSolve(sketch);
        }
        {
            var Q0;
            Q0=makeQuery(id+"F16.imprint","IMPRINT",FACE,{"disambiguationData":[TD([[makeQuery(id+"F16.imprint","IMPRINT",EDGE,{"derivedFrom":makeQuery(id+"F1.opExtrude","CAP_EDGE",EDGE,{"disambiguationData":[OSD([sQuery(id+"F0.wireOp",EDGE,"E1.left")])],"isStart":true})}),-1.0]])]});
            var Q1;
            {var subQ1=sQuery(id+"F16.wireOp",EDGE,"E89.MirrorCS");Q1=makeQuery(id+"F16.imprint","IMPRINT",FACE,{"disambiguationData":[TD([[makeQuery(id+"F16.imprint","IMPRINT",EDGE,{"derivedFrom":subQ1}),-1.0]])]});}
            var Q2;
            Q2=makeQuery(id+"F16.imprint","IMPRINT",FACE,{"disambiguationData":[TD([[makeQuery(id+"F16.imprint","IMPRINT",EDGE,{"derivedFrom":sQuery(id+"F16.wireOp",EDGE,"E80")}),-1.0]])]});
            var Q3;
            Q3=makeQuery(id+"F2.opExtrude","CAP_FACE",FACE,{"disambiguationData":[OSD([sQuery(id+"F0.wireOp",EDGE,"E12"),sQuery(id+"F0.wireOp",EDGE,"E13"),sQuery(id+"F0.wireOp",EDGE,"E14"),sQuery(id+"F0.wireOp",EDGE,"E15"),sQuery(id+"F0.wireOp",EDGE,"E17.filletArc"),sQuery(id+"F0.wireOp",EDGE,"E18.filletArc"),sQuery(id+"F0.wireOp",EDGE,"E19.filletArc"),sQuery(id+"F0.wireOp",EDGE,"E20.filletArc"),sQuery(id+"F0.wireOp",EDGE,"E25.0"),sQuery(id+"F0.wireOp",EDGE,"E25.1"),sQuery(id+"F0.wireOp",EDGE,"E25.2"),sQuery(id+"F0.wireOp",EDGE,"E25.3"),sQuery(id+"F0.wireOp",EDGE,"E25.4"),sQuery(id+"F0.wireOp",EDGE,"E25.5"),sQuery(id+"F0.wireOp",EDGE,"E25.6"),sQuery(id+"F0.wireOp",EDGE,"E25.7")])],"isStart":false});
            extrude(context, id + "F17", {"entities" : qUnion([Q0, Q1, Q2]), "endBound" : BoundingType.UP_TO_SURFACE, "depth" : 25.4 * mm, "endBoundEntityFace" : qUnion([Q3]), "offsetDistance" : 25.4 * mm});
        }
    });
